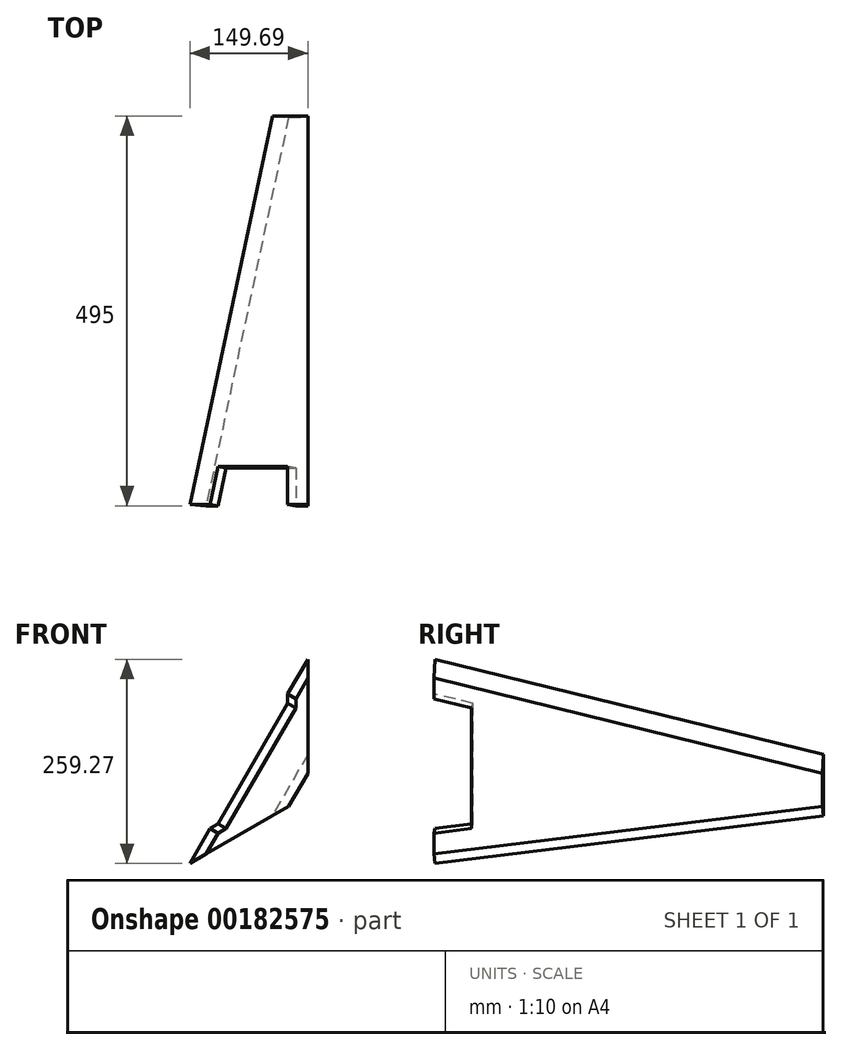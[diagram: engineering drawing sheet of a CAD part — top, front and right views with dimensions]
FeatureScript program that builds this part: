
annotation { "Feature Type Name" : "Feature", "Feature Type Description" : "" }
export const myFeature = defineFeature(function(context is Context, id is Id, definition is map)
    precondition{}
    {
        {
            var Q0;
            Q0=qCreatedBy(makeId("Top.planeOp"),FACE);
            var sketch = newSketch(context, id + "F0", { "sketchPlane" : qUnion([Q0])});
            skLineSegment(sketch, "E0", {"start": v(-150, 0) * mm, "end": v(150, 0) * mm, "construction": true});
            skLineSegment(sketch, "E1", {"start": v(0, 0) * mm, "end": v(0, 495) * mm, "construction": true});
            skLineSegment(sketch, "E2", {"start": v(-45, 495) * mm, "end": v(45, 495) * mm, "construction": true});
            skSolve(sketch);
        }
        {
            var Q0;
            Q0=qCreatedBy(makeId("Front.planeOp"),FACE);
            var sketch = newSketch(context, id + "F1", { "sketchPlane" : qUnion([Q0])});
            skCircle(sketch, "E3.cCircle", {"center": v(0, 0) * mm, "radius": 86.6 * mm, "construction": true});
            skLineSegment(sketch, "E3.0", {"start": v(150, -86.6) * mm, "end": v(-150, -86.6) * mm});
            skLineSegment(sketch, "E3.1", {"start": v(-150, -86.6) * mm, "end": v(0, 173.2) * mm});
            skLineSegment(sketch, "E3.2", {"start": v(0, 173.2) * mm, "end": v(150, -86.6) * mm});
            skPoint(sketch, "E3.0.midPoint", {"position": v(0, -86.6) * mm});
            skSolve(sketch);
        }
        {
            var Q0;
            Q0=sQuery(id+"F0.wireOp",EDGE,"E2");
            cPoint(context, id + "F2", {"entities" : qUnion([Q0]), "parameter" : 0.5});
        }
        {
            var Q0;
            Q0 = qCreatedBy(id + "F2" ,VERTEX);
            var Q1;
            Q1=sQuery(id+"F0.wireOp",EDGE,"E1");
            cPlane(context, id + "F3", {"entities" : qUnion([Q0, Q1]), "cplaneType" : CPlaneType.LINE_POINT, "offset" : 25 * mm, "width" : 150 * mm, "height" : 150 * mm});
        }
        {
            var Q0;
            Q0=qCreatedBy(id+"F3.planeOp",FACE);
            var sketch = newSketch(context, id + "F4", { "sketchPlane" : qUnion([Q0])});
            skCircle(sketch, "E4.cCircle", {"center": v(0, 0) * mm, "radius": 25.98 * mm, "construction": true});
            skLineSegment(sketch, "E4.0", {"start": v(45, -25.98) * mm, "end": v(-45, -25.98) * mm});
            skLineSegment(sketch, "E4.1", {"start": v(-45, -25.98) * mm, "end": v(0, 51.96) * mm});
            skLineSegment(sketch, "E4.2", {"start": v(0, 51.96) * mm, "end": v(45, -25.98) * mm});
            skPoint(sketch, "E4.0.midPoint", {"position": v(0, -25.98) * mm});
            skSolve(sketch);
        }
        {
            var Q0;
            Q0=makeQuery(id+"F1.imprint","IMPRINT",FACE,{"disambiguationData":[TD([[makeQuery(id+"F1.imprint","IMPRINT",EDGE,{"derivedFrom":sQuery(id+"F1.wireOp",EDGE,"E3.0")}),-1.0]])]});
            var Q1;
            Q1=makeQuery(id+"F4.imprint","IMPRINT",FACE,{"disambiguationData":[TD([[makeQuery(id+"F4.imprint","IMPRINT",EDGE,{"derivedFrom":sQuery(id+"F4.wireOp",EDGE,"E4.0")}),-1.0]])]});
            loft(context, id + "F5", {"sheetProfilesArray" : [{ "sheetProfileEntities" : qUnion([Q0]) }, { "sheetProfileEntities" : qUnion([Q1]) }]});
        }
        {
            var Q0;
            {var subQ0=sQuery(id+"F4.wireOp",EDGE,"E4.2");var subQ1=sQuery(id+"F4.wireOp",EDGE,"E4.1");var subQ2=sQuery(id+"F4.wireOp",EDGE,"E4.0");var subQ3=sQuery(id+"F1.wireOp",EDGE,"E3.1");var subQ4=sQuery(id+"F1.wireOp",EDGE,"E3.2");var subQ5=sQuery(id+"F1.wireOp",EDGE,"E3.0");Q0=makeQuery(id+"F5.opLoft","SWEPT_FACE",FACE,{"disambiguationData":[OSD([subQ5,subQ3,subQ4,subQ2,subQ1,subQ0]),TDD([makeQuery(id+"F1.imprint","INTERSECT",VERTEX,{"derivedFrom":[subQ5,subQ3]}),makeQuery(id+"F1.imprint","INTERSECT",VERTEX,{"derivedFrom":[subQ3,subQ4]}),makeQuery(id+"F1.imprint","IMPRINT",EDGE,{"derivedFrom":subQ3}),makeQuery(id+"F4.imprint","INTERSECT",VERTEX,{"derivedFrom":[subQ2,subQ0]}),makeQuery(id+"F4.imprint","INTERSECT",VERTEX,{"derivedFrom":[subQ1,subQ0]}),makeQuery(id+"F4.imprint","IMPRINT",EDGE,{"derivedFrom":subQ0})])]});}
            cPlane(context, id + "F6", {"entities" : qUnion([Q0]), "cplaneType" : CPlaneType.OFFSET, "offset" : 12 * mm, "oppositeDirection" : true, "width" : 150 * mm, "height" : 150 * mm});
        }
        {
            var Q0;
            Q0=qCreatedBy(id+"F6.planeOp",FACE);
            var sketch = newSketch(context, id + "F7", { "sketchPlane" : qUnion([Q0])});
            skCircle(sketch, "E5", {"center": v(-271.41, 0) * mm, "radius": 342.02 * mm});
            skSolve(sketch);
        }
        {
            var Q0;
            Q0=makeQuery(id+"F7.imprint","IMPRINT",FACE,{"disambiguationData":[TD([[makeQuery(id+"F7.imprint","IMPRINT",EDGE,{"derivedFrom":sQuery(id+"F7.wireOp",EDGE,"E5")}),1.0]])]});
            var Q1;
            Q1=sQuery(id+"F7.wireOp",EDGE,"E5");
            extrude(context, id + "F8", {"entities" : qUnion([Q0]), "operationType" : NewBodyOperationType.REMOVE, "surfaceEntities" : qUnion([Q1]), "endBound" : BoundingType.THROUGH_ALL, "oppositeDirection" : true, "depth" : 25 * mm});
        }
        {
            var Q0;
            {var subQ0=sQuery(id+"F4.wireOp",EDGE,"E4.2");var subQ1=sQuery(id+"F4.wireOp",EDGE,"E4.1");var subQ2=sQuery(id+"F4.wireOp",EDGE,"E4.0");var subQ3=sQuery(id+"F1.wireOp",EDGE,"E3.1");var subQ4=sQuery(id+"F1.wireOp",EDGE,"E3.2");var subQ5=sQuery(id+"F1.wireOp",EDGE,"E3.0");Q0=makeQuery(id+"F5.opLoft","SWEPT_FACE",FACE,{"disambiguationData":[OSD([subQ5,subQ3,subQ4,subQ2,subQ1,subQ0]),TDD([makeQuery(id+"F1.imprint","INTERSECT",VERTEX,{"derivedFrom":[subQ5,subQ3]}),makeQuery(id+"F1.imprint","INTERSECT",VERTEX,{"derivedFrom":[subQ3,subQ4]}),makeQuery(id+"F1.imprint","IMPRINT",EDGE,{"derivedFrom":subQ3}),makeQuery(id+"F4.imprint","INTERSECT",VERTEX,{"derivedFrom":[subQ2,subQ0]}),makeQuery(id+"F4.imprint","INTERSECT",VERTEX,{"derivedFrom":[subQ1,subQ0]}),makeQuery(id+"F4.imprint","IMPRINT",EDGE,{"derivedFrom":subQ0})])]});}
            var sketch = newSketch(context, id + "F9", { "sketchPlane" : qUnion([Q0])});
            skLineSegment(sketch, "E6", {"start": v(10.53, -98.9) * mm, "end": v(-39.47, -88.38) * mm});
            skLineSegment(sketch, "E7", {"start": v(-39.47, -88.38) * mm, "end": v(-39.47, 88.38) * mm});
            skLineSegment(sketch, "E8", {"start": v(-39.47, 88.38) * mm, "end": v(10.53, 98.9) * mm});
            skLineSegment(sketch, "E9", {"start": v(10.53, -98.9) * mm, "end": v(10.53, 98.9) * mm});
            skSolve(sketch);
        }
        {
            var Q0;
            Q0 = qSketchRegion(id + "F9", true);
            extrude(context, id + "F10", {"entities" : qUnion([Q0]), "operationType" : NewBodyOperationType.REMOVE, "endBound" : BoundingType.THROUGH_ALL, "oppositeDirection" : true, "depth" : 25 * mm});
        }
        {
            var Q0;
            Q0=makeQuery(id+"F8.boolean.opBoolean","COPY",FACE,{"derivedFrom":makeQuery(id+"F8.opExtrude","CAP_FACE",FACE,{"disambiguationData":[OSD([sQuery(id+"F7.wireOp",EDGE,"E5")])],"isStart":true})});
            var sketch = newSketch(context, id + "F11", { "sketchPlane" : qUnion([Q0])});
            skLineSegment(sketch, "E10.bottom", {"start": v(-9.06, 172.78) * mm, "end": v(-72.03, 172.78) * mm});
            skLineSegment(sketch, "E10.top", {"start": v(-9.06, -235.1) * mm, "end": v(-72.03, -235.1) * mm});
            skLineSegment(sketch, "E10.left", {"start": v(-9.06, 172.78) * mm, "end": v(-9.06, -235.1) * mm});
            skLineSegment(sketch, "E10.right", {"start": v(-72.03, 172.78) * mm, "end": v(-72.03, -235.1) * mm});
            skSolve(sketch);
        }
        {
            var Q0;
            Q0 = qSketchRegion(id + "F11", true);
            extrude(context, id + "F12", {"entities" : qUnion([Q0]), "operationType" : NewBodyOperationType.REMOVE, "endBound" : BoundingType.THROUGH_ALL, "oppositeDirection" : true, "depth" : 25 * mm});
        }
        {
            var Q0;
            {var subQ0=sQuery(id+"F4.wireOp",EDGE,"E4.2");var subQ1=sQuery(id+"F4.wireOp",EDGE,"E4.1");var subQ2=sQuery(id+"F4.wireOp",EDGE,"E4.0");var subQ3=sQuery(id+"F1.wireOp",EDGE,"E3.1");var subQ4=sQuery(id+"F1.wireOp",EDGE,"E3.2");var subQ5=sQuery(id+"F1.wireOp",EDGE,"E3.0");Q0=makeQuery(id+"F5.opLoft","SWEPT_FACE",FACE,{"disambiguationData":[OSD([subQ5,subQ3,subQ4,subQ2,subQ1,subQ0]),TDD([makeQuery(id+"F1.imprint","INTERSECT",VERTEX,{"derivedFrom":[subQ5,subQ3]}),makeQuery(id+"F1.imprint","INTERSECT",VERTEX,{"derivedFrom":[subQ3,subQ4]}),makeQuery(id+"F1.imprint","IMPRINT",EDGE,{"derivedFrom":subQ3}),makeQuery(id+"F4.imprint","INTERSECT",VERTEX,{"derivedFrom":[subQ2,subQ0]}),makeQuery(id+"F4.imprint","INTERSECT",VERTEX,{"derivedFrom":[subQ1,subQ0]}),makeQuery(id+"F4.imprint","IMPRINT",EDGE,{"derivedFrom":subQ0})])]});}
            var sketch = newSketch(context, id + "F13", { "sketchPlane" : qUnion([Q0])});
            skLineSegment(sketch, "E11.bottom", {"start": v(-488.17, -45) * mm, "end": v(-516.2, -45) * mm});
            skLineSegment(sketch, "E11.top", {"start": v(-488.17, 45) * mm, "end": v(-516.2, 45) * mm});
            skLineSegment(sketch, "E11.left", {"start": v(-488.17, -45) * mm, "end": v(-488.17, 45) * mm});
            skLineSegment(sketch, "E11.right", {"start": v(-516.2, -45) * mm, "end": v(-516.2, 45) * mm});
            skSolve(sketch);
        }
        {
            var Q0;
            Q0 = qSketchRegion(id + "F13", true);
            extrude(context, id + "F14", {"entities" : qUnion([Q0]), "operationType" : NewBodyOperationType.REMOVE, "endBound" : BoundingType.THROUGH_ALL, "oppositeDirection" : true, "depth" : 25 * mm});
        }
        {
            var Q0;
            Q0=qCreatedBy(id+"F3.planeOp",FACE);
            var sketch = newSketch(context, id + "F15", { "sketchPlane" : qUnion([Q0])});
            skLineSegment(sketch, "E12.0", {"start": v(-45, -25.98) * mm, "end": v(0, 51.96) * mm});
            skLineSegment(sketch, "E13.0", {"start": v(0, 51.96) * mm, "end": v(45, -25.98) * mm});
            skLineSegment(sketch, "E14", {"start": v(0, 51.96) * mm, "end": v(0, 0) * mm});
            skLineSegment(sketch, "E15", {"start": v(0, 0) * mm, "end": v(45, -25.98) * mm});
            skSolve(sketch);
        }
        {
            var Q0;
            Q0=sQuery(id+"F15.wireOp",EDGE,"E15");
            var Q1;
            Q1=makeQuery(id+"F5.opLoft","SWEPT_EDGE",EDGE,{"disambiguationData":[OSD([sQuery(id+"F1.wireOp",EDGE,"E3.0"),sQuery(id+"F1.wireOp",EDGE,"E3.1"),sQuery(id+"F4.wireOp",EDGE,"E4.0"),sQuery(id+"F4.wireOp",EDGE,"E4.2")])]});
            cPlane(context, id + "F16", {"entities" : qUnion([Q0, Q1]), "cplaneType" : CPlaneType.LINE_ANGLE, "offset" : 25 * mm, "angle" : 0 * degree, "width" : 150 * mm, "height" : 150 * mm});
        }
        {
            var Q0;
            Q0=qCreatedBy(id+"F16.planeOp",FACE);
            var sketch = newSketch(context, id + "F17", { "sketchPlane" : qUnion([Q0])});
            skCircle(sketch, "E16", {"center": v(-73.88, -254.32) * mm, "radius": 326.8 * mm});
            skSolve(sketch);
        }
        {
            var Q0;
            Q0 = qSketchRegion(id + "F17", true);
            extrude(context, id + "F18", {"entities" : qUnion([Q0]), "operationType" : NewBodyOperationType.REMOVE, "endBound" : BoundingType.THROUGH_ALL, "depth" : 25 * mm});
        }
        {
            var Q0;
            Q0=sQuery(id+"F15.wireOp",EDGE,"E14");
            var Q1;
            Q1=makeQuery(id+"F5.opLoft","SWEPT_EDGE",EDGE,{"disambiguationData":[OSD([sQuery(id+"F1.wireOp",EDGE,"E3.1"),sQuery(id+"F1.wireOp",EDGE,"E3.2"),sQuery(id+"F4.wireOp",EDGE,"E4.1"),sQuery(id+"F4.wireOp",EDGE,"E4.2")])]});
            cPlane(context, id + "F19", {"entities" : qUnion([Q0, Q1]), "cplaneType" : CPlaneType.LINE_ANGLE, "offset" : 25 * mm, "angle" : 0 * degree, "width" : 150 * mm, "height" : 150 * mm});
        }
        {
            var Q0;
            Q0=qCreatedBy(id+"F19.planeOp",FACE);
            var sketch = newSketch(context, id + "F20", { "sketchPlane" : qUnion([Q0])});
            skCircle(sketch, "E17", {"center": v(244.28, 80.67) * mm, "radius": 344.65 * mm});
            skSolve(sketch);
        }
        {
            var Q0;
            Q0 = qSketchRegion(id + "F20", true);
            extrude(context, id + "F21", {"entities" : qUnion([Q0]), "operationType" : NewBodyOperationType.REMOVE, "endBound" : BoundingType.THROUGH_ALL, "depth" : 25 * mm});
        }
    });
